# Revit family: NAU_Naughtone_Stng_Fiji1
name_source: partatom
category: Furniture
revit_build: Autodesk Revit 2015 (Build: 20140903_1530(x64)
units: mm (PartAtom-declared; Revit-internal decimal feet)

## types (1)
- Fiji Lounge Chair
    Assembly Code = E2020200
    AssetType = Movable
    BIMObjectName = NAU_Naughtone_Seating_Fiji
    Category = Pr_40_50_12_48 : Lounge chairs
    Color = Various
    Description = Fiji Lounge Chair
    DurationUnit = year
    Finish = Upholstered
    IfcExportAs = IfcFurnishingElementType
    IfcExportType = CHAIR
    Keynote = Pr_40_50_12_48
    MainColor = Various
    ManufacturerAddress = "Knaresborough Tech Park, Manse Lane, Knaresborough, HG5 8LF"
    ManufacturerName = Naughtone
    ManufacturerURL = www.naughtone.com
    Material = Timber/foam
    Model = FIJICH
    ModelNumber = FIJICH
    ModelReference = Fiji Lounge Chair
    NBSDescription = Seating
    NBSReference = 45-35-72/352
    Name = Seating_Fiji_Naughtone
    NominalHeight = 885 mm
    NominalLength = 865 mm
    NominalWidth = 850 mm
    ProductInformation = www.naughtone.com/products/fiji/
    Shape = Rectangular
    Size = 865 x 850 x 885mm
    SustainabilityPerformance = FISP certified. ISO 14001. SCS indoor advantage gold
    URL = www.naughtone.com
    Uniclass2015Code = Pr_40_50_12_48
    Uniclass2015Title = Lounge chairs
    Uniclass2015Version = Products v1.10
    Version = 1
    WarrantyDescription = Request warranty information from naughtone
    WarrantyDurationLabor = 5
    WarrantyDurationParts = 5
    WarrantyDurationUnit = year

## geometry (parser evidence)
native form markers: Sweep x2
no freeform markers — native parametric forms only
